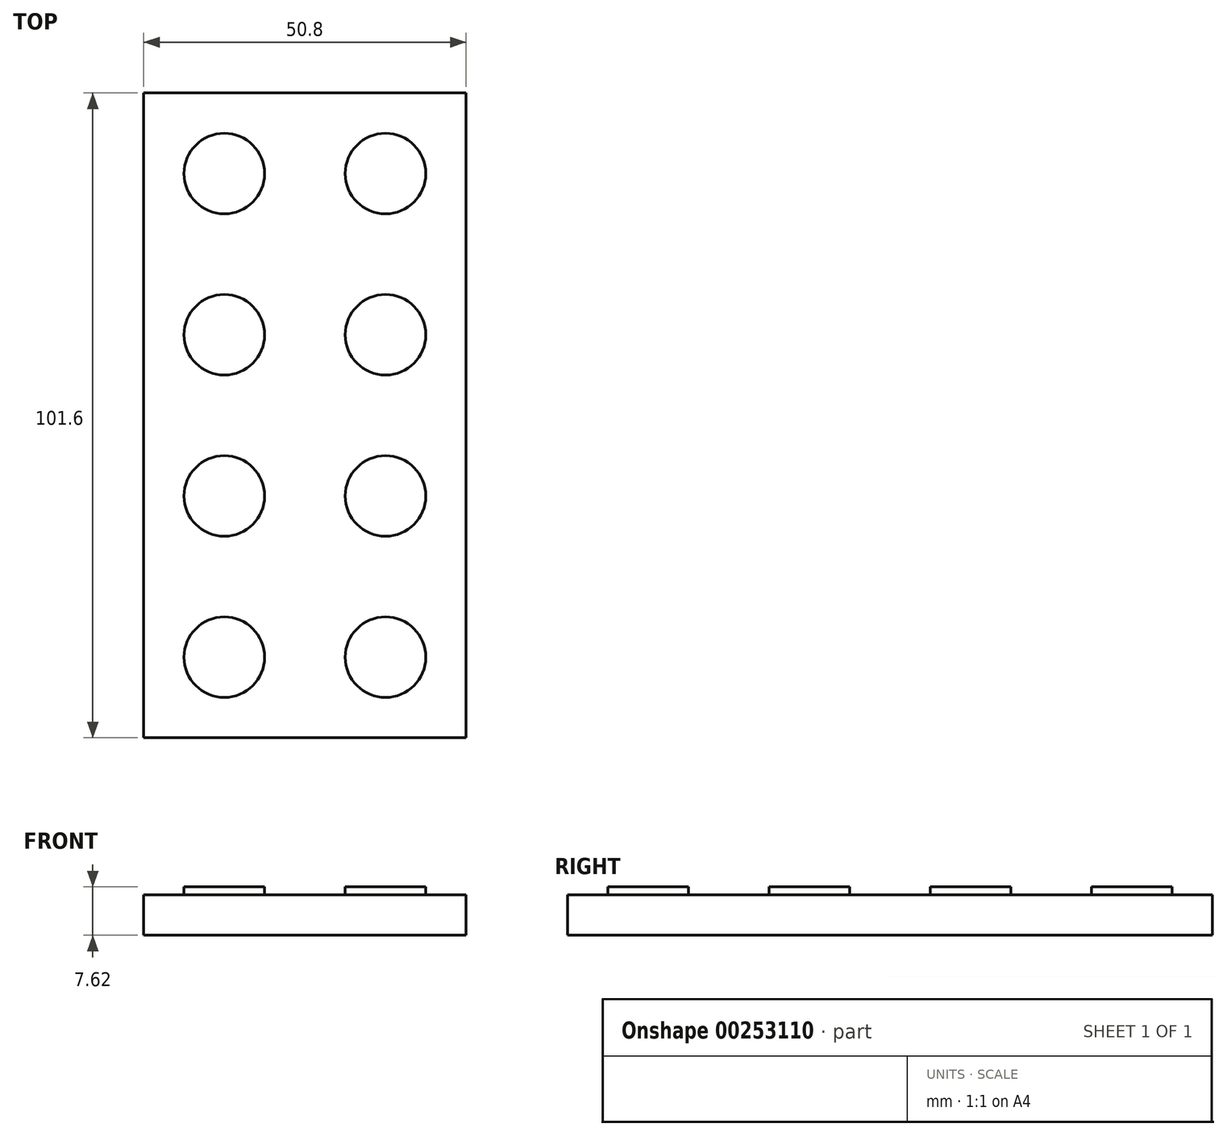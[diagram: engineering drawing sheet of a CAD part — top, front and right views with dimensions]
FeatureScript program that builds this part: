
annotation { "Feature Type Name" : "Feature", "Feature Type Description" : "" }
export const myFeature = defineFeature(function(context is Context, id is Id, definition is map)
    precondition{}
    {
        {
            var Q0;
            Q0=qCreatedBy(makeId("Top.planeOp"),FACE);
            var sketch = newSketch(context, id + "F0", { "sketchPlane" : qUnion([Q0])});
            skLineSegment(sketch, "E0.bottom", {"start": v(-4.25, 38.1) * mm, "end": v(46.55, 38.1) * mm});
            skLineSegment(sketch, "E0.top", {"start": v(-4.25, -63.5) * mm, "end": v(46.55, -63.5) * mm});
            skLineSegment(sketch, "E0.left", {"start": v(-4.25, 38.1) * mm, "end": v(-4.25, -63.5) * mm});
            skLineSegment(sketch, "E0.right", {"start": v(46.55, 38.1) * mm, "end": v(46.55, -63.5) * mm});
            skLineSegment(sketch, "E1", {"start": v(-4.25, 38.1) * mm, "end": v(-4.25, 25.4) * mm});
            skLineSegment(sketch, "E2", {"start": v(-4.25, 25.4) * mm, "end": v(-4.25, 0) * mm});
            skLineSegment(sketch, "E3", {"start": v(-4.25, 0) * mm, "end": v(-4.25, -25.4) * mm});
            skLineSegment(sketch, "E4", {"start": v(-4.25, -25.4) * mm, "end": v(-4.25, -50.8) * mm});
            skLineSegment(sketch, "E5", {"start": v(-4.25, 38.1) * mm, "end": v(8.45, 38.1) * mm});
            skLineSegment(sketch, "E6", {"start": v(8.45, 38.1) * mm, "end": v(33.85, 38.1) * mm});
            skCircle(sketch, "E7", {"center": v(8.45, 25.4) * mm, "radius": 6.35 * mm});
            skCircle(sketch, "E8", {"center": v(33.85, 25.4) * mm, "radius": 6.35 * mm});
            skCircle(sketch, "E9", {"center": v(33.85, 0) * mm, "radius": 6.35 * mm});
            skCircle(sketch, "E10", {"center": v(8.45, 0) * mm, "radius": 6.35 * mm});
            skCircle(sketch, "E11", {"center": v(8.45, -25.4) * mm, "radius": 6.35 * mm});
            skCircle(sketch, "E12", {"center": v(8.45, -50.8) * mm, "radius": 6.35 * mm});
            skCircle(sketch, "E13", {"center": v(33.85, -25.4) * mm, "radius": 6.35 * mm});
            skCircle(sketch, "E14", {"center": v(33.85, -50.8) * mm, "radius": 6.35 * mm});
            skSolve(sketch);
        }
        {
            var Q0;
            Q0 = qSketchRegion(id + "F0", true);
            extrude(context, id + "F1", {"entities" : qUnion([Q0]), "depth" : 6.35 * mm});
        }
        {
            var Q0;
            Q0=makeQuery(id+"F0.imprint","IMPRINT",FACE,{"disambiguationData":[TD([[makeQuery(id+"F0.imprint","IMPRINT",EDGE,{"derivedFrom":sQuery(id+"F0.wireOp",EDGE,"E14")}),1.0]])]});
            var Q1;
            Q1=makeQuery(id+"F0.imprint","IMPRINT",FACE,{"disambiguationData":[TD([[makeQuery(id+"F0.imprint","IMPRINT",EDGE,{"derivedFrom":sQuery(id+"F0.wireOp",EDGE,"E12")}),1.0]])]});
            var Q2;
            Q2=makeQuery(id+"F0.imprint","IMPRINT",FACE,{"disambiguationData":[TD([[makeQuery(id+"F0.imprint","IMPRINT",EDGE,{"derivedFrom":sQuery(id+"F0.wireOp",EDGE,"E11")}),1.0]])]});
            var Q3;
            Q3=makeQuery(id+"F0.imprint","IMPRINT",FACE,{"disambiguationData":[TD([[makeQuery(id+"F0.imprint","IMPRINT",EDGE,{"derivedFrom":sQuery(id+"F0.wireOp",EDGE,"E13")}),1.0]])]});
            var Q4;
            Q4=makeQuery(id+"F0.imprint","IMPRINT",FACE,{"disambiguationData":[TD([[makeQuery(id+"F0.imprint","IMPRINT",EDGE,{"derivedFrom":sQuery(id+"F0.wireOp",EDGE,"E9")}),1.0]])]});
            var Q5;
            Q5=makeQuery(id+"F0.imprint","IMPRINT",FACE,{"disambiguationData":[TD([[makeQuery(id+"F0.imprint","IMPRINT",EDGE,{"derivedFrom":sQuery(id+"F0.wireOp",EDGE,"E10")}),1.0]])]});
            var Q6;
            Q6=makeQuery(id+"F0.imprint","IMPRINT",FACE,{"disambiguationData":[TD([[makeQuery(id+"F0.imprint","IMPRINT",EDGE,{"derivedFrom":sQuery(id+"F0.wireOp",EDGE,"E7")}),1.0]])]});
            var Q7;
            Q7=makeQuery(id+"F0.imprint","IMPRINT",FACE,{"disambiguationData":[TD([[makeQuery(id+"F0.imprint","IMPRINT",EDGE,{"derivedFrom":sQuery(id+"F0.wireOp",EDGE,"E8")}),1.0]])]});
            extrude(context, id + "F2", {"entities" : qUnion([Q0, Q1, Q2, Q3, Q4, Q5, Q6, Q7]), "operationType" : NewBodyOperationType.ADD, "depth" : 7.62 * mm});
        }
    });
